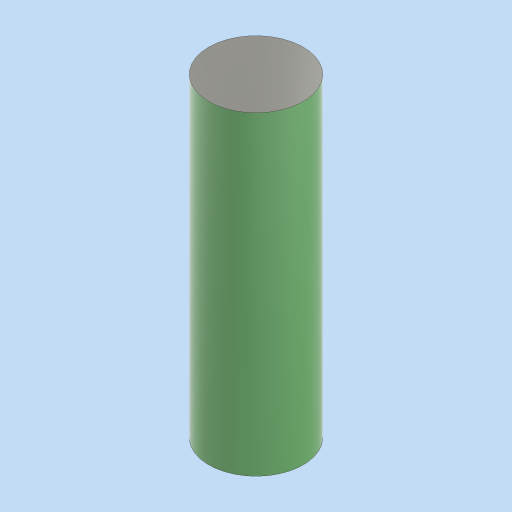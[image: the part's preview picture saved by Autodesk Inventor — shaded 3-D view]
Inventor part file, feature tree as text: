
AUTODESK INVENTOR PART (.ipt)
format: ipt  version: 2023 (Build 270158000, 158)  size: 92,672 bytes
history: native  units: in
note: dims shown in document units (in); Inventor stores cm internally (conversion verified against a paired STEP export)
features: extrude x1, sketch x1
ambient origin geometry x8: Origin, YZ Plane, XZ Plane, XY Plane, X Axis, Y Axis, Z Axis, Center Point
bodies: Solid1 (feature_tree)
feature tree (2):
  extrude  "Extrusion1"  Depth=2.7559in TaperAngle=0.0deg
  sketch  "Sketch1"  dims[d0=0.8268in d1=2.7559in d2=0.0in]
